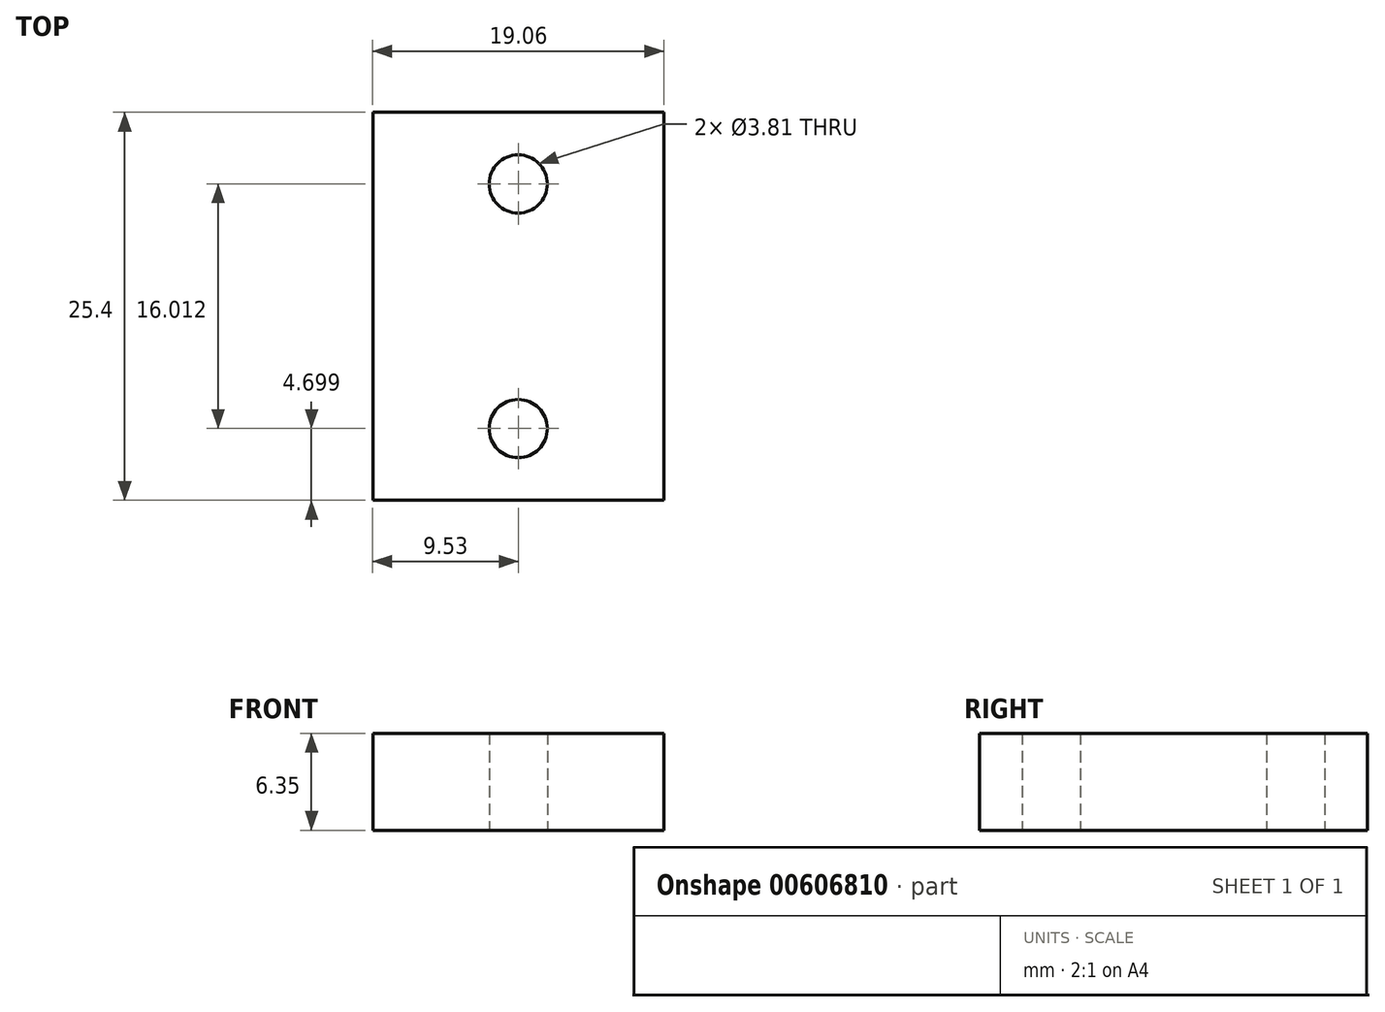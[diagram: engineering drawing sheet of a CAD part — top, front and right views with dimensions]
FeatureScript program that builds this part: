
annotation { "Feature Type Name" : "Feature", "Feature Type Description" : "" }
export const myFeature = defineFeature(function(context is Context, id is Id, definition is map)
    precondition{}
    {
        {
            var Q0;
            Q0=qCreatedBy(makeId("Top.planeOp"),FACE);
            var sketch = newSketch(context, id + "F0", { "sketchPlane" : qUnion([Q0])});
            skLineSegment(sketch, "E0.bottom", {"start": v(9.53, -12.7) * mm, "end": v(-9.53, -12.7) * mm});
            skLineSegment(sketch, "E0.top", {"start": v(9.53, 12.7) * mm, "end": v(-9.52, 12.7) * mm});
            skLineSegment(sketch, "E0.left", {"start": v(9.53, -12.7) * mm, "end": v(9.53, 12.7) * mm});
            skLineSegment(sketch, "E0.right", {"start": v(-9.53, -12.7) * mm, "end": v(-9.52, 12.7) * mm});
            skPoint(sketch, "E0.middle", {"position": v(0, 0) * mm});
            skCircle(sketch, "E1", {"center": v(0, 8.01) * mm, "radius": 1.9 * mm});
            skCircle(sketch, "E2", {"center": v(0, -8) * mm, "radius": 1.9 * mm});
            skSolve(sketch);
        }
        {
            var Q0;
            Q0=makeQuery(id+"F0.imprint","IMPRINT",FACE,{"disambiguationData":[TD([[makeQuery(id+"F0.imprint","IMPRINT",EDGE,{"derivedFrom":sQuery(id+"F0.wireOp",EDGE,"E0.bottom")}),-1.0]])]});
            extrude(context, id + "F1", {"entities" : qUnion([Q0]), "depth" : 6.35 * mm, "offsetDistance" : 25.4 * mm});
        }
    });
